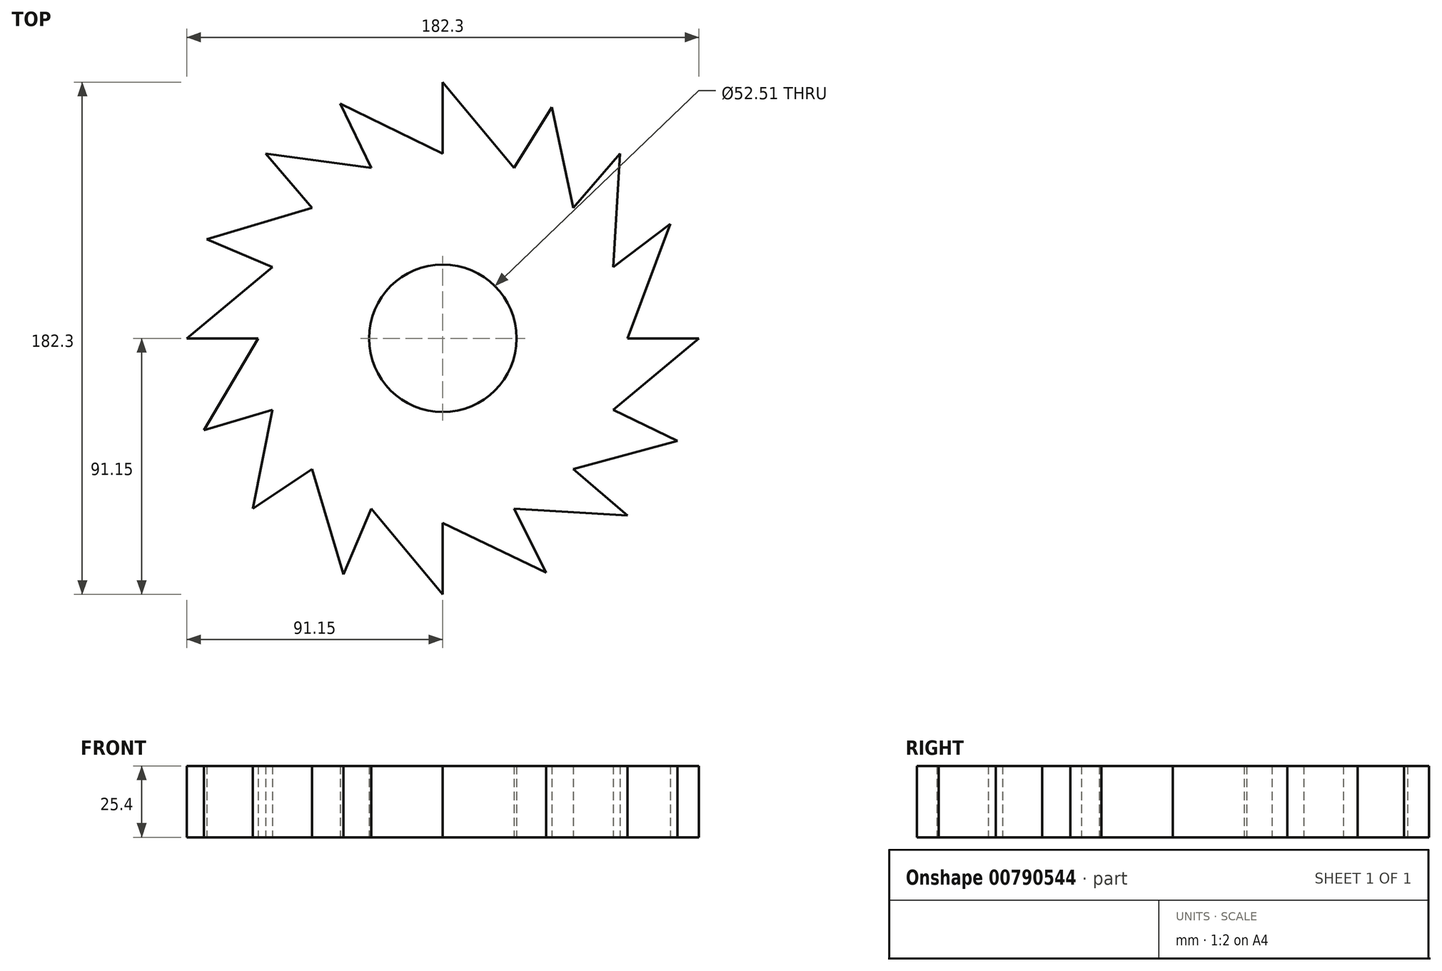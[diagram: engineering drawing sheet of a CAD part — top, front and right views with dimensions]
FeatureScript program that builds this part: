
annotation { "Feature Type Name" : "Feature", "Feature Type Description" : "" }
export const myFeature = defineFeature(function(context is Context, id is Id, definition is map)
    precondition{}
    {
        {
            var Q0;
            Q0=qCreatedBy(makeId("Top.planeOp"),FACE);
            var sketch = newSketch(context, id + "F0", { "sketchPlane" : qUnion([Q0])});
            skCircle(sketch, "E0", {"center": v(0, 0) * mm, "radius": 65.75 * mm});
            skCircle(sketch, "E1", {"center": v(0, 0) * mm, "radius": 26.25 * mm});
            skPoint(sketch, "E2", {"position": v(0, 65.75) * mm});
            skPoint(sketch, "E3", {"position": v(-65.75, 0) * mm});
            skPoint(sketch, "E4", {"position": v(65.75, 0) * mm});
            skPoint(sketch, "E5", {"position": v(0, -65.75) * mm});
            skPoint(sketch, "E6", {"position": v(-46.5, 46.5) * mm});
            skPoint(sketch, "E7", {"position": v(46.5, 46.5) * mm});
            skPoint(sketch, "E8", {"position": v(46.5, -46.5) * mm});
            skPoint(sketch, "E9", {"position": v(-46.5, -46.5) * mm});
            skPoint(sketch, "E10", {"position": v(-25.4, 60.64) * mm});
            skPoint(sketch, "E11", {"position": v(25.4, 60.64) * mm});
            skPoint(sketch, "E12", {"position": v(25.4, -60.64) * mm});
            skPoint(sketch, "E13", {"position": v(-25.4, -60.64) * mm});
            skPoint(sketch, "E14", {"position": v(-60.64, 25.4) * mm});
            skPoint(sketch, "E15", {"position": v(60.64, 25.4) * mm});
            skPoint(sketch, "E16", {"position": v(60.64, -25.4) * mm});
            skPoint(sketch, "E17", {"position": v(-60.64, -25.4) * mm});
            skLineSegment(sketch, "E18", {"start": v(0, 65.75) * mm, "end": v(0, 91.15) * mm});
            skLineSegment(sketch, "E19", {"start": v(0, 91.15) * mm, "end": v(25.4, 60.64) * mm});
            skLineSegment(sketch, "E20", {"start": v(25.4, 60.64) * mm, "end": v(38.83, 82.2) * mm});
            skLineSegment(sketch, "E21", {"start": v(38.83, 82.2) * mm, "end": v(46.5, 46.5) * mm});
            skLineSegment(sketch, "E22", {"start": v(46.5, 46.5) * mm, "end": v(63.05, 65.75) * mm});
            skLineSegment(sketch, "E23", {"start": v(63.05, 65.75) * mm, "end": v(60.64, 25.4) * mm});
            skLineSegment(sketch, "E24", {"start": v(60.64, 25.4) * mm, "end": v(80.93, 40.68) * mm});
            skLineSegment(sketch, "E25", {"start": v(80.93, 40.68) * mm, "end": v(65.75, 0) * mm});
            skLineSegment(sketch, "E26", {"start": v(91.15, 0) * mm, "end": v(60.64, -25.4) * mm});
            skLineSegment(sketch, "E27", {"start": v(60.64, -25.4) * mm, "end": v(83.51, -36.45) * mm});
            skLineSegment(sketch, "E28", {"start": v(83.51, -36.45) * mm, "end": v(46.5, -46.5) * mm});
            skLineSegment(sketch, "E29", {"start": v(46.5, -46.5) * mm, "end": v(65.75, -63.05) * mm});
            skLineSegment(sketch, "E30", {"start": v(65.75, -63.05) * mm, "end": v(25.4, -60.64) * mm});
            skLineSegment(sketch, "E31", {"start": v(25.4, -60.64) * mm, "end": v(36.76, -83.36) * mm});
            skLineSegment(sketch, "E32", {"start": v(36.76, -83.36) * mm, "end": v(0, -65.75) * mm});
            skLineSegment(sketch, "E33", {"start": v(0, -65.75) * mm, "end": v(0, -91.15) * mm});
            skLineSegment(sketch, "E34", {"start": v(0, -91.15) * mm, "end": v(-25.4, -60.64) * mm});
            skLineSegment(sketch, "E35", {"start": v(-25.4, -60.64) * mm, "end": v(-35.3, -84.04) * mm});
            skLineSegment(sketch, "E36", {"start": v(-35.3, -84.04) * mm, "end": v(-46.5, -46.5) * mm});
            skLineSegment(sketch, "E37", {"start": v(-46.5, -46.5) * mm, "end": v(-67.58, -60.64) * mm});
            skLineSegment(sketch, "E38", {"start": v(-67.58, -60.64) * mm, "end": v(-60.64, -25.4) * mm});
            skLineSegment(sketch, "E39", {"start": v(-60.64, -25.4) * mm, "end": v(-85, -32.63) * mm});
            skLineSegment(sketch, "E40", {"start": v(-85, -32.63) * mm, "end": v(-65.75, 0) * mm});
            skLineSegment(sketch, "E41", {"start": v(-65.75, 0) * mm, "end": v(-91.15, 0) * mm});
            skLineSegment(sketch, "E42", {"start": v(-91.15, 0) * mm, "end": v(-60.64, 25.4) * mm});
            skLineSegment(sketch, "E43", {"start": v(-60.64, 25.4) * mm, "end": v(-84.04, 35.3) * mm});
            skLineSegment(sketch, "E44", {"start": v(-84.04, 35.3) * mm, "end": v(-46.5, 46.5) * mm});
            skLineSegment(sketch, "E45", {"start": v(-46.5, 46.5) * mm, "end": v(-63.05, 65.75) * mm});
            skLineSegment(sketch, "E46", {"start": v(-63.05, 65.75) * mm, "end": v(-25.4, 60.64) * mm});
            skLineSegment(sketch, "E47", {"start": v(-25.4, 60.64) * mm, "end": v(-36.47, 83.5) * mm});
            skLineSegment(sketch, "E48", {"start": v(-36.47, 83.5) * mm, "end": v(0, 65.75) * mm});
            skLineSegment(sketch, "E49", {"start": v(65.75, 0) * mm, "end": v(91.15, 0) * mm});
            skSolve(sketch);
        }
        {
            var Q0;
            Q0=makeQuery(id+"F0.imprint","IMPRINT",FACE,{"disambiguationData":[TD([[makeQuery(id+"F0.imprint","IMPRINT",EDGE,{"derivedFrom":sQuery(id+"F0.wireOp",EDGE,"E1")}),-1.0]])]});
            var Q1;
            {var subQ0=sQuery(id+"F0.wireOp",EDGE,"E45");Q1=makeQuery(id+"F0.imprint","IMPRINT",FACE,{"disambiguationData":[TD([[makeQuery(id+"F0.imprint","IMPRINT",EDGE,{"derivedFrom":subQ0}),-1.0]])]});}
            var Q2;
            {var subQ0=sQuery(id+"F0.wireOp",EDGE,"E43");Q2=makeQuery(id+"F0.imprint","IMPRINT",FACE,{"disambiguationData":[TD([[makeQuery(id+"F0.imprint","IMPRINT",EDGE,{"derivedFrom":subQ0}),-1.0]])]});}
            var Q3;
            {var subQ0=sQuery(id+"F0.wireOp",EDGE,"E41");Q3=makeQuery(id+"F0.imprint","IMPRINT",FACE,{"disambiguationData":[TD([[makeQuery(id+"F0.imprint","IMPRINT",EDGE,{"derivedFrom":subQ0}),-1.0]])]});}
            var Q4;
            {var subQ0=sQuery(id+"F0.wireOp",EDGE,"E39");Q4=makeQuery(id+"F0.imprint","IMPRINT",FACE,{"disambiguationData":[TD([[makeQuery(id+"F0.imprint","IMPRINT",EDGE,{"derivedFrom":subQ0}),-1.0]])]});}
            var Q5;
            {var subQ0=sQuery(id+"F0.wireOp",EDGE,"E37");Q5=makeQuery(id+"F0.imprint","IMPRINT",FACE,{"disambiguationData":[TD([[makeQuery(id+"F0.imprint","IMPRINT",EDGE,{"derivedFrom":subQ0}),-1.0]])]});}
            var Q6;
            {var subQ0=sQuery(id+"F0.wireOp",EDGE,"E35");Q6=makeQuery(id+"F0.imprint","IMPRINT",FACE,{"disambiguationData":[TD([[makeQuery(id+"F0.imprint","IMPRINT",EDGE,{"derivedFrom":subQ0}),-1.0]])]});}
            var Q7;
            {var subQ0=sQuery(id+"F0.wireOp",EDGE,"E33");Q7=makeQuery(id+"F0.imprint","IMPRINT",FACE,{"disambiguationData":[TD([[makeQuery(id+"F0.imprint","IMPRINT",EDGE,{"derivedFrom":subQ0}),-1.0]])]});}
            var Q8;
            {var subQ0=sQuery(id+"F0.wireOp",EDGE,"E31");Q8=makeQuery(id+"F0.imprint","IMPRINT",FACE,{"disambiguationData":[TD([[makeQuery(id+"F0.imprint","IMPRINT",EDGE,{"derivedFrom":subQ0}),-1.0]])]});}
            var Q9;
            {var subQ0=sQuery(id+"F0.wireOp",EDGE,"E29");Q9=makeQuery(id+"F0.imprint","IMPRINT",FACE,{"disambiguationData":[TD([[makeQuery(id+"F0.imprint","IMPRINT",EDGE,{"derivedFrom":subQ0}),-1.0]])]});}
            var Q10;
            {var subQ0=sQuery(id+"F0.wireOp",EDGE,"E27");Q10=makeQuery(id+"F0.imprint","IMPRINT",FACE,{"disambiguationData":[TD([[makeQuery(id+"F0.imprint","IMPRINT",EDGE,{"derivedFrom":subQ0}),-1.0]])]});}
            var Q11;
            {var subQ2=sQuery(id+"F0.wireOp",EDGE,"E26");Q11=makeQuery(id+"F0.imprint","IMPRINT",FACE,{"disambiguationData":[TD([[makeQuery(id+"F0.imprint","IMPRINT",EDGE,{"derivedFrom":subQ2}),-1.0]])]});}
            var Q12;
            {var subQ0=sQuery(id+"F0.wireOp",EDGE,"E24");Q12=makeQuery(id+"F0.imprint","IMPRINT",FACE,{"disambiguationData":[TD([[makeQuery(id+"F0.imprint","IMPRINT",EDGE,{"derivedFrom":subQ0}),-1.0]])]});}
            var Q13;
            {var subQ0=sQuery(id+"F0.wireOp",EDGE,"E22");Q13=makeQuery(id+"F0.imprint","IMPRINT",FACE,{"disambiguationData":[TD([[makeQuery(id+"F0.imprint","IMPRINT",EDGE,{"derivedFrom":subQ0}),-1.0]])]});}
            var Q14;
            {var subQ0=sQuery(id+"F0.wireOp",EDGE,"E20");Q14=makeQuery(id+"F0.imprint","IMPRINT",FACE,{"disambiguationData":[TD([[makeQuery(id+"F0.imprint","IMPRINT",EDGE,{"derivedFrom":subQ0}),-1.0]])]});}
            var Q15;
            {var subQ0=sQuery(id+"F0.wireOp",EDGE,"E18");Q15=makeQuery(id+"F0.imprint","IMPRINT",FACE,{"disambiguationData":[TD([[makeQuery(id+"F0.imprint","IMPRINT",EDGE,{"derivedFrom":subQ0}),-1.0]])]});}
            var Q16;
            {var subQ2=sQuery(id+"F0.wireOp",EDGE,"E47");Q16=makeQuery(id+"F0.imprint","IMPRINT",FACE,{"disambiguationData":[TD([[makeQuery(id+"F0.imprint","IMPRINT",EDGE,{"derivedFrom":subQ2}),-1.0]])]});}
            extrude(context, id + "F1", {"entities" : qUnion([Q0, Q1, Q2, Q3, Q4, Q5, Q6, Q7, Q8, Q9, Q10, Q11, Q12, Q13, Q14, Q15, Q16]), "depth" : 25.4 * mm, "offsetDistance" : 25.4 * mm});
        }
    });
